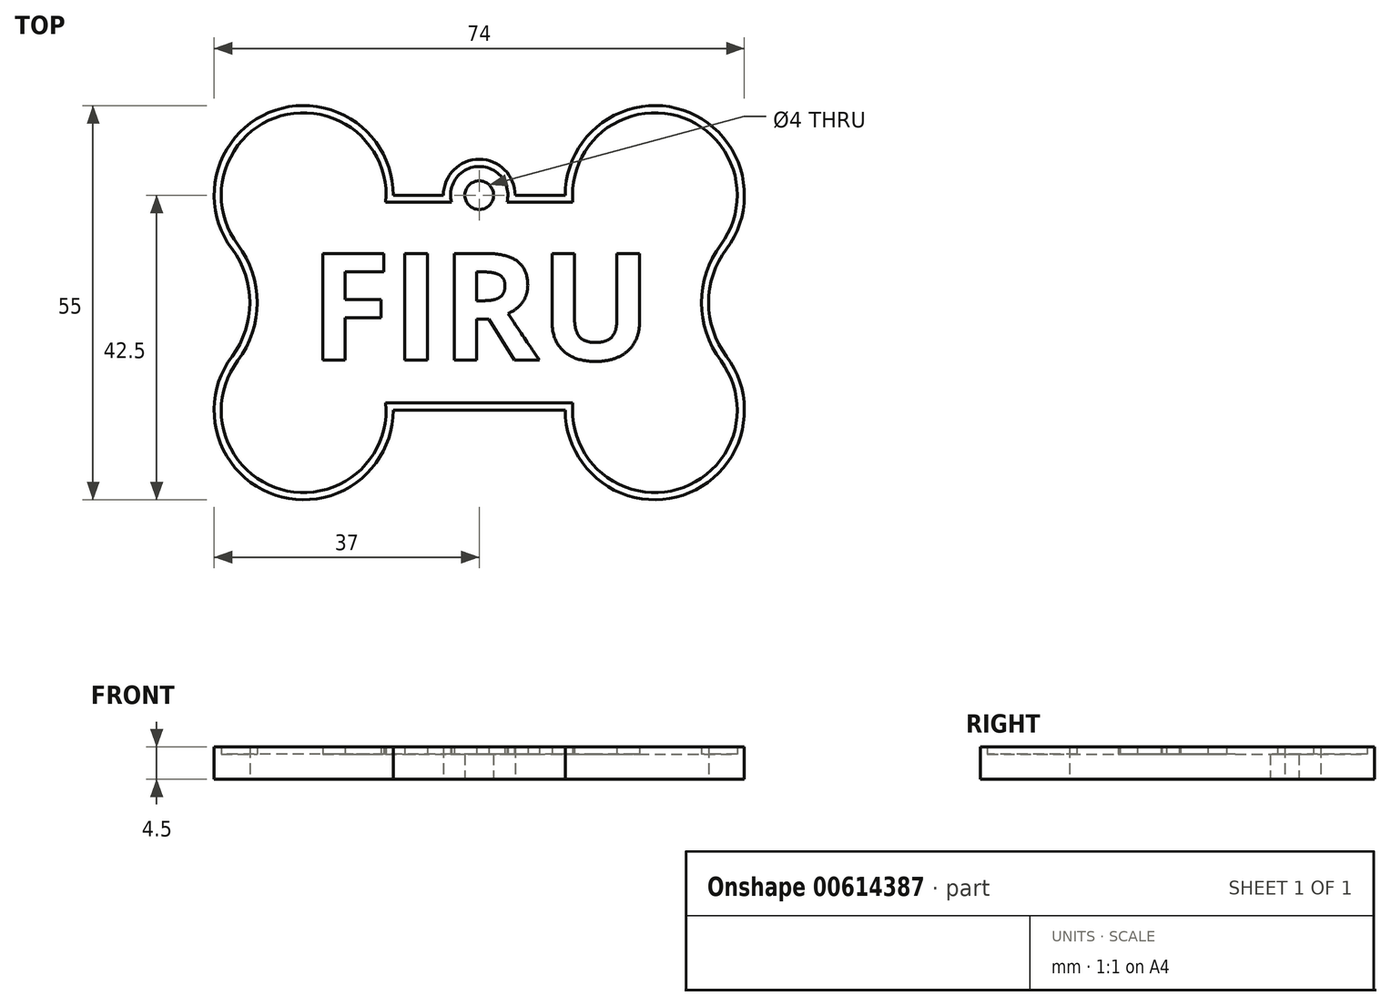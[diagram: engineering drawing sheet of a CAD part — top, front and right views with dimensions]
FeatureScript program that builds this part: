
annotation { "Feature Type Name" : "Feature", "Feature Type Description" : "" }
export const myFeature = defineFeature(function(context is Context, id is Id, definition is map)
    precondition{}
    {
        {
            var Q0;
            Q0=qCreatedBy(makeId("Top.planeOp"),FACE);
            var sketch = newSketch(context, id + "F0", { "sketchPlane" : qUnion([Q0])});
            skLineSegment(sketch, "E0", {"start": v(22.5, 30) * mm, "end": v(29.5, 30) * mm});
            skArc(sketch, "E1", {"start": v(22.5, 30) * mm, "mid": v(6.05, 41.86) * mm, "end": v(0, 22.5) * mm});
            skArc(sketch, "E2", {"start": v(0, 7.5) * mm, "mid": v(6.05, -11.86) * mm, "end": v(22.5, 0) * mm});
            skArc(sketch, "E3", {"start": v(46.5, 0) * mm, "mid": v(62.95, -11.86) * mm, "end": v(69, 7.5) * mm});
            skArc(sketch, "E4", {"start": v(69, 22.5) * mm, "mid": v(62.95, 41.86) * mm, "end": v(46.5, 30) * mm});
            skArc(sketch, "E5", {"start": v(0, 7.5) * mm, "mid": v(2.5, 15) * mm, "end": v(0, 22.5) * mm});
            skPoint(sketch, "E5.first.point", {"position": v(0, 22.5) * mm});
            skPoint(sketch, "E5.second.point", {"position": v(0, 7.5) * mm});
            skPoint(sketch, "E5.third.point", {"position": v(-22.5, 15) * mm});
            skPoint(sketch, "E5.third.point.positionSnap0", {"position": v(0, 15) * mm});
            skArc(sketch, "E6", {"start": v(69, 22.5) * mm, "mid": v(66.5, 15) * mm, "end": v(69, 7.5) * mm});
            skPoint(sketch, "E6.first.point", {"position": v(69, 22.5) * mm});
            skPoint(sketch, "E6.second.point", {"position": v(69, 7.5) * mm});
            skPoint(sketch, "E6.third.point", {"position": v(91.5, 14.72) * mm});
            skLineSegment(sketch, "E7.trimOffspring", {"start": v(59, 30) * mm, "end": v(60, 30) * mm});
            skLineSegment(sketch, "E8.trimOffspring", {"start": v(59, 0) * mm, "end": v(69, 0) * mm});
            skLineSegment(sketch, "E9.trimOffspring", {"start": v(22.5, 0) * mm, "end": v(46.5, 0) * mm});
            skPoint(sketch, "E10.start.orphan", {"position": v(0, 0) * mm});
            skPoint(sketch, "E11.orphan", {"position": v(0, 30) * mm});
            skCircle(sketch, "E12", {"center": v(34.5, 30) * mm, "radius": 2 * mm});
            skLineSegment(sketch, "E13.trimOffspring", {"start": v(39.5, 30) * mm, "end": v(46.5, 30) * mm});
            skArc(sketch, "E14", {"start": v(39.5, 30) * mm, "mid": v(34.5, 35) * mm, "end": v(29.5, 30) * mm});
            skSolve(sketch);
        }
        {
            var Q0;
            Q0=makeQuery(id+"F0.imprint","IMPRINT",FACE,{"disambiguationData":[TD([[makeQuery(id+"F0.imprint","IMPRINT",EDGE,{"derivedFrom":sQuery(id+"F0.wireOp",EDGE,"E0")}),-1.0]])]});
            extrude(context, id + "F1", {"entities" : qUnion([Q0]), "depth" : 3.5 * mm, "offsetDistance" : 25 * mm});
        }
        {
            var Q0;
            Q0=makeQuery(id+"F1.opExtrude","CAP_FACE",FACE,{"disambiguationData":[OSD([sQuery(id+"F0.wireOp",EDGE,"E0"),sQuery(id+"F0.wireOp",EDGE,"E1"),sQuery(id+"F0.wireOp",EDGE,"E2"),sQuery(id+"F0.wireOp",EDGE,"E3"),sQuery(id+"F0.wireOp",EDGE,"E4"),sQuery(id+"F0.wireOp",EDGE,"E5"),sQuery(id+"F0.wireOp",EDGE,"E6"),sQuery(id+"F0.wireOp",EDGE,"E9.trimOffspring"),sQuery(id+"F0.wireOp",EDGE,"E12"),sQuery(id+"F0.wireOp",EDGE,"E13.trimOffspring"),sQuery(id+"F0.wireOp",EDGE,"E14")])],"isStart":false});
            var sketch = newSketch(context, id + "F2", { "sketchPlane" : qUnion([Q0])});
            skText(sketch, "E15", { "text": "FIRU", "fontName": "OpenSans-Bold.ttf"});
            skArc(sketch, "E16.0", {"start": v(47.54, 1) * mm, "mid": v(62.16, -11.06) * mm, "end": v(68.2, 6.9) * mm});
            skLineSegment(sketch, "E16.1", {"start": v(21.46, 1) * mm, "end": v(47.54, 1) * mm});
            skArc(sketch, "E16.2", {"start": v(68.2, 6.9) * mm, "mid": v(65.5, 15) * mm, "end": v(68.2, 23.1) * mm});
            skArc(sketch, "E16.3", {"start": v(0.8, 6.9) * mm, "mid": v(6.84, -11.06) * mm, "end": v(21.46, 1) * mm});
            skArc(sketch, "E16.4", {"start": v(0.8, 23.1) * mm, "mid": v(3.5, 15) * mm, "end": v(0.8, 6.9) * mm});
            skArc(sketch, "E16.5", {"start": v(21.46, 29) * mm, "mid": v(6.84, 41.06) * mm, "end": v(0.8, 23.1) * mm});
            skArc(sketch, "E16.6", {"start": v(68.2, 23.1) * mm, "mid": v(62.16, 41.06) * mm, "end": v(47.54, 29) * mm});
            skLineSegment(sketch, "E16.7", {"start": v(47.54, 29) * mm, "end": v(38.37, 29) * mm});
            skArc(sketch, "E16.8", {"start": v(38.37, 29) * mm, "mid": v(34.5, 34) * mm, "end": v(30.63, 29) * mm});
            skLineSegment(sketch, "E16.9", {"start": v(30.63, 29) * mm, "end": v(21.46, 29) * mm});
            const initialGuessF2  = {"E15": [0.0108, 0.007, 1, 0, 0.015]};
            skSetInitialGuess(sketch, initialGuessF2);
            skSolve(sketch);
        }
        {
            var Q0;
            Q0=makeQuery(id+"F2.imprint","IMPRINT",FACE,{"disambiguationData":[TD([[makeQuery(id+"F2.imprint","IMPRINT",EDGE,{"derivedFrom":sQuery(id+"F2.wireOp",EDGE,"E16.0")}),-1.0]])]});
            var Q1;
            Q1=makeQuery(id+"F2.imprint","IMPRINT",FACE,{"disambiguationData":[TD([[makeQuery(id+"F2.imprint","IMPRINT",EDGE,{"derivedFrom":sQuery(id+"F2.wireOp",EDGE,"E15.sketch_text.stroke-33")}),-1.0]])]});
            var Q2;
            Q2=makeQuery(id+"F2.imprint","IMPRINT",FACE,{"disambiguationData":[TD([[makeQuery(id+"F2.imprint","IMPRINT",EDGE,{"derivedFrom":sQuery(id+"F2.wireOp",EDGE,"E15.sketch_text.stroke-14")}),-1.0]])]});
            var Q3;
            Q3=makeQuery(id+"F2.imprint","IMPRINT",FACE,{"disambiguationData":[TD([[makeQuery(id+"F2.imprint","IMPRINT",EDGE,{"derivedFrom":sQuery(id+"F2.wireOp",EDGE,"E15.sketch_text.stroke-10")}),-1.0]])]});
            var Q4;
            Q4=makeQuery(id+"F2.imprint","IMPRINT",FACE,{"disambiguationData":[TD([[makeQuery(id+"F2.imprint","IMPRINT",EDGE,{"derivedFrom":sQuery(id+"F2.wireOp",EDGE,"E15.sketch_text.stroke-0")}),-1.0]])]});
            extrude(context, id + "F3", {"entities" : qUnion([Q0, Q1, Q2, Q3, Q4]), "operationType" : NewBodyOperationType.ADD, "depth" : 1 * mm, "offsetDistance" : 25 * mm});
        }
    });
